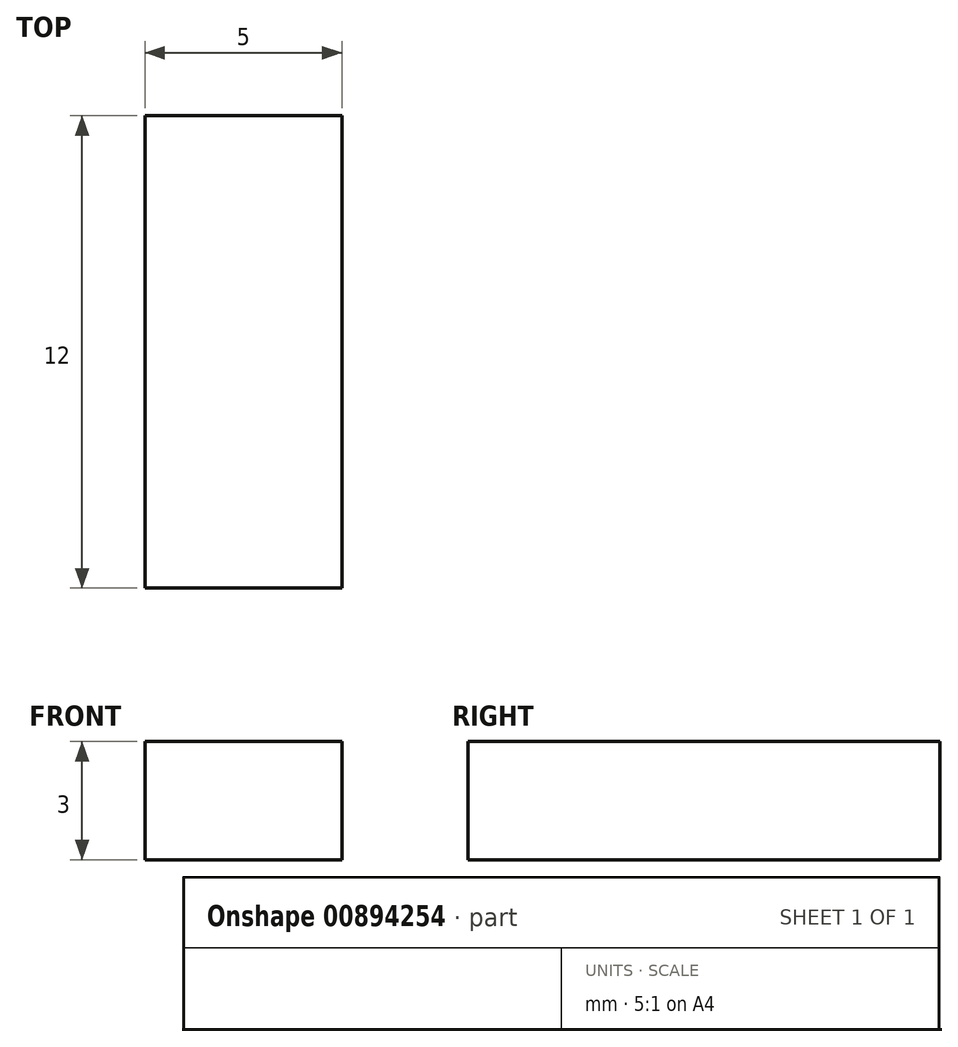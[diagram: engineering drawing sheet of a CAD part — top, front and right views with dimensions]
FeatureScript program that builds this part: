
annotation { "Feature Type Name" : "Feature", "Feature Type Description" : "" }
export const myFeature = defineFeature(function(context is Context, id is Id, definition is map)
    precondition{}
    {
        {
            var Q0;
            Q0=qCreatedBy(makeId("Front.planeOp"),FACE);
            var sketch = newSketch(context, id + "F0", { "sketchPlane" : qUnion([Q0])});
            skLineSegment(sketch, "E0.bottom", {"start": v(0, 0) * mm, "end": v(5, 0) * mm});
            skLineSegment(sketch, "E0.top", {"start": v(0, 3) * mm, "end": v(5, 3) * mm});
            skLineSegment(sketch, "E0.left", {"start": v(0, 0) * mm, "end": v(0, 3) * mm});
            skLineSegment(sketch, "E0.right", {"start": v(5, 0) * mm, "end": v(5, 3) * mm});
            skSolve(sketch);
        }
        {
            var Q0;
            Q0 = qSketchRegion(id + "F0", true);
            extrude(context, id + "F1", {"entities" : qUnion([Q0]), "depth" : 12 * mm, "offsetDistance" : 25 * mm});
        }
    });
